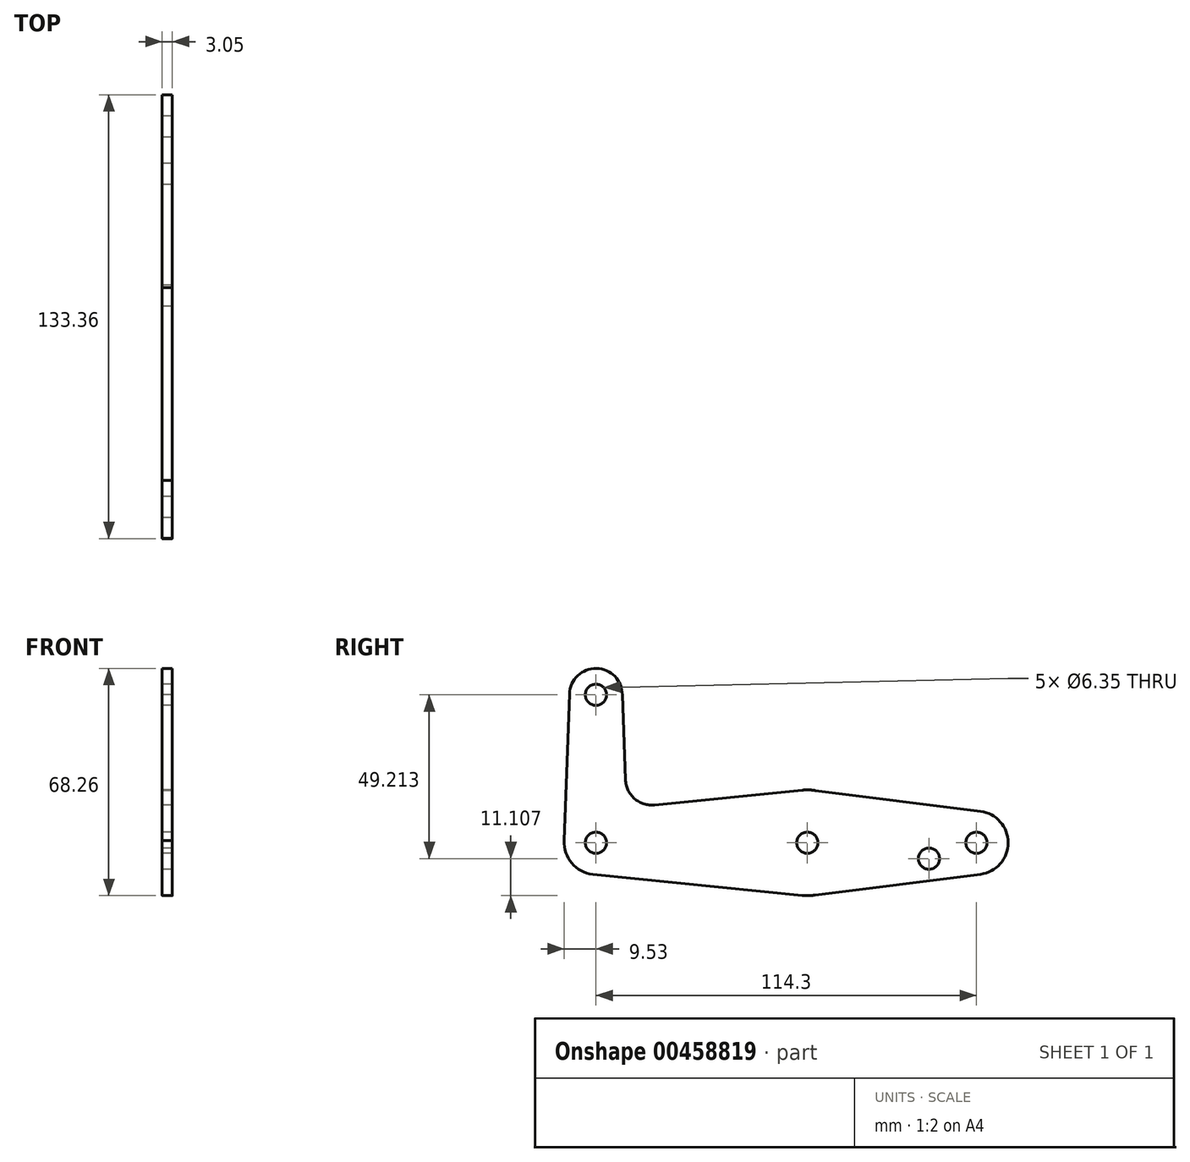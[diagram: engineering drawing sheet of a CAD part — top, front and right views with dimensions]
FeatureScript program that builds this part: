
annotation { "Feature Type Name" : "Feature", "Feature Type Description" : "" }
export const myFeature = defineFeature(function(context is Context, id is Id, definition is map)
    precondition{}
    {
        {
            var Q0;
            Q0=qCreatedBy(makeId("Right.planeOp"),FACE);
            var sketch = newSketch(context, id + "F0", { "sketchPlane" : qUnion([Q0])});
            skCircle(sketch, "E0", {"center": v(0, 0) * mm, "radius": 9.53 * mm});
            skCircle(sketch, "E1", {"center": v(63.5, 0) * mm, "radius": 15.88 * mm});
            skCircle(sketch, "E2", {"center": v(114.3, 0) * mm, "radius": 9.53 * mm});
            skCircle(sketch, "E3", {"center": v(0, 44.45) * mm, "radius": 7.94 * mm});
            skLineSegment(sketch, "E4", {"start": v(114.3, 0) * mm, "end": v(0, 0) * mm, "construction": true});
            skLineSegment(sketch, "E5", {"start": v(0, 0) * mm, "end": v(0, 44.45) * mm, "construction": true});
            skLineSegment(sketch, "E6", {"start": v(65.09, -15.8) * mm, "end": v(115.49, -9.45) * mm});
            skLineSegment(sketch, "E7", {"start": v(115.49, 9.45) * mm, "end": v(65.09, 15.8) * mm});
            skLineSegment(sketch, "E8", {"start": v(61.91, -15.8) * mm, "end": v(-1.22, -9.45) * mm});
            skLineSegment(sketch, "E9", {"start": v(61.91, 15.8) * mm, "end": v(17.6, 11.34) * mm});
            skLineSegment(sketch, "E10", {"start": v(-9.53, 0) * mm, "end": v(-7.93, 44.73) * mm});
            skLineSegment(sketch, "E11", {"start": v(7.94, 44.45) * mm, "end": v(8.85, 18.97) * mm});
            skCircle(sketch, "E12", {"center": v(100.03, -4.76) * mm, "radius": 3.18 * mm});
            skCircle(sketch, "E13", {"center": v(114.3, 0) * mm, "radius": 3.18 * mm});
            skCircle(sketch, "E14", {"center": v(63.5, 0) * mm, "radius": 3.18 * mm});
            skCircle(sketch, "E15", {"center": v(0, 0) * mm, "radius": 3.18 * mm});
            skCircle(sketch, "E16", {"center": v(0, 44.45) * mm, "radius": 3.18 * mm});
            skPoint(sketch, "E17.newPointA", {"position": v(-1.22, 9.45) * mm});
            skPoint(sketch, "E17.newPointB", {"position": v(9.53, 0) * mm});
            skArc(sketch, "E17.filletArc", {"start": v(8.85, 18.97) * mm, "mid": v(11.57, 13.26) * mm, "end": v(17.6, 11.34) * mm});
            skSolve(sketch);
        }
        {
            var Q0;
            Q0 = qSketchRegion(id + "F0", true);
            extrude(context, id + "F1", {"entities" : qUnion([Q0]), "depth" : 3.05 * mm});
        }
    });
